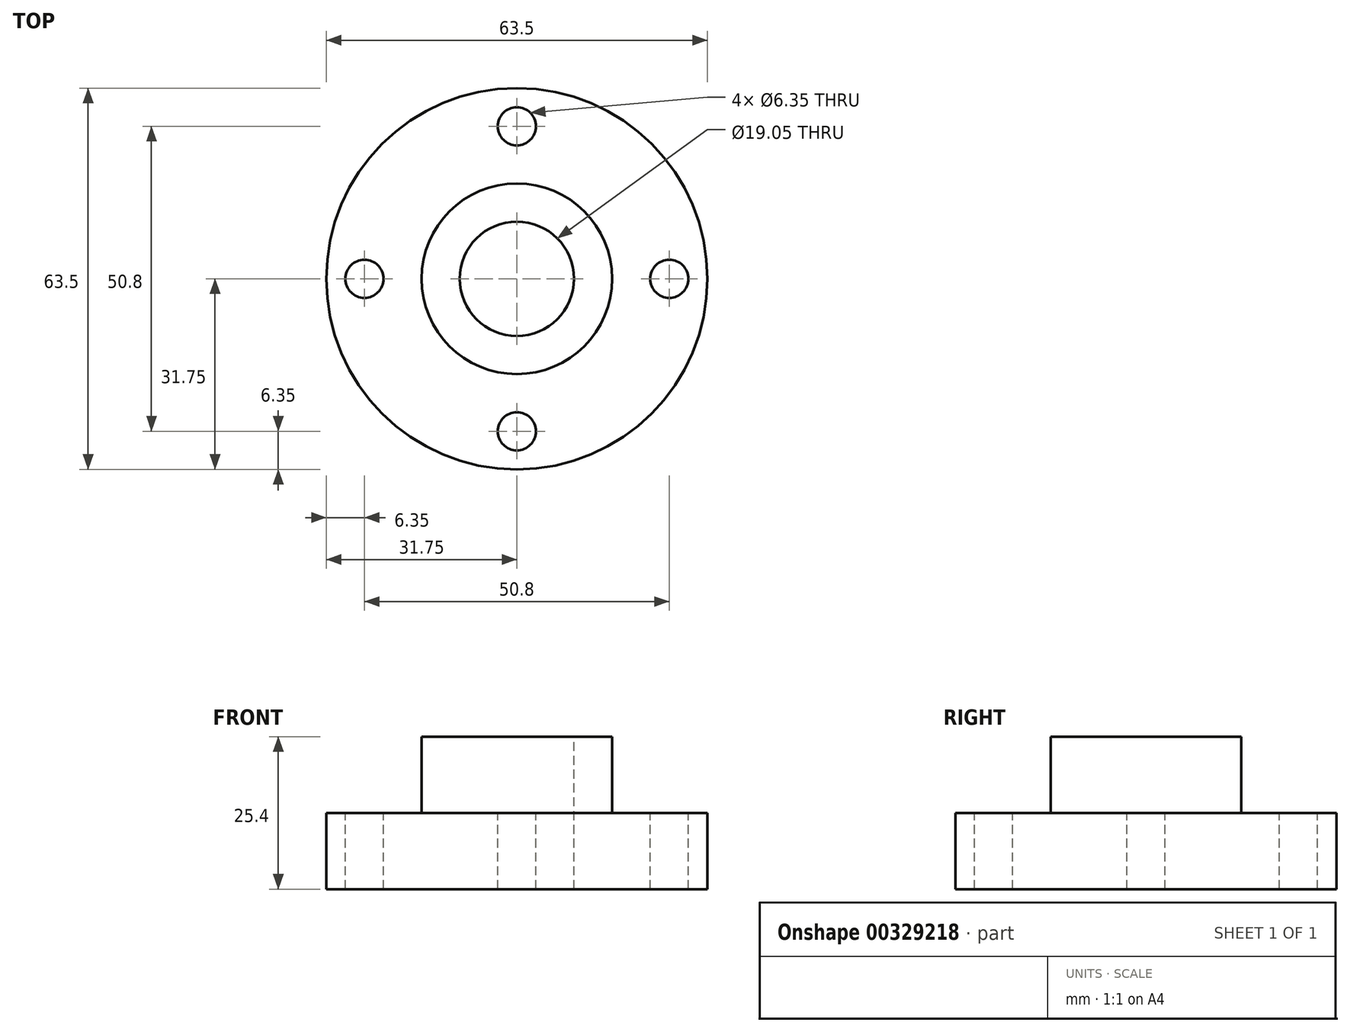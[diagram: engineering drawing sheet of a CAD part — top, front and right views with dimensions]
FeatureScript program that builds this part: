
annotation { "Feature Type Name" : "Feature", "Feature Type Description" : "" }
export const myFeature = defineFeature(function(context is Context, id is Id, definition is map)
    precondition{}
    {
        {
            var Q0;
            Q0=qCreatedBy(makeId("Front.planeOp"),FACE);
            var sketch = newSketch(context, id + "F0", { "sketchPlane" : qUnion([Q0])});
            skLineSegment(sketch, "E0.bottom", {"start": v(0, 0) * mm, "end": v(63.5, 0) * mm});
            skLineSegment(sketch, "E0.top", {"start": v(0, 12.7) * mm, "end": v(63.5, 12.7) * mm});
            skLineSegment(sketch, "E0.left", {"start": v(0, 0) * mm, "end": v(0, 12.7) * mm});
            skLineSegment(sketch, "E0.right", {"start": v(63.5, 0) * mm, "end": v(63.5, 12.7) * mm});
            skLineSegment(sketch, "E1.bottom", {"start": v(15.88, 12.7) * mm, "end": v(47.62, 12.7) * mm});
            skLineSegment(sketch, "E1.top", {"start": v(15.87, 25.4) * mm, "end": v(47.62, 25.4) * mm});
            skLineSegment(sketch, "E1.left", {"start": v(15.88, 12.7) * mm, "end": v(15.87, 25.4) * mm});
            skLineSegment(sketch, "E1.right", {"start": v(47.62, 12.7) * mm, "end": v(47.62, 25.4) * mm});
            skSolve(sketch);
        }
        {
            var Q0;
            Q0=qCreatedBy(makeId("Top.planeOp"),FACE);
            var sketch = newSketch(context, id + "F1", { "sketchPlane" : qUnion([Q0])});
            skCircle(sketch, "E2", {"center": v(0, 0) * mm, "radius": 31.75 * mm});
            skSolve(sketch);
        }
        {
            var Q0;
            Q0 = qSketchRegion(id + "F1", true);
            extrude(context, id + "F2", {"entities" : qUnion([Q0]), "depth" : 12.7 * mm});
        }
        {
            var Q0;
            Q0=makeQuery(id+"F2.opExtrude","CAP_FACE",FACE,{"disambiguationData":[OSD([sQuery(id+"F1.wireOp",EDGE,"E2")])],"isStart":false});
            var sketch = newSketch(context, id + "F3", { "sketchPlane" : qUnion([Q0])});
            skCircle(sketch, "E3", {"center": v(0, 0) * mm, "radius": 15.88 * mm});
            skSolve(sketch);
        }
        {
            var Q0;
            Q0 = qSketchRegion(id + "F3", true);
            extrude(context, id + "F4", {"entities" : qUnion([Q0]), "operationType" : NewBodyOperationType.ADD, "depth" : 12.7 * mm});
        }
        {
            var Q0;
            Q0=makeQuery(id+"F4.opExtrude","CAP_FACE",FACE,{"disambiguationData":[OSD([sQuery(id+"F3.wireOp",EDGE,"E3")])],"isStart":false});
            var sketch = newSketch(context, id + "F5", { "sketchPlane" : qUnion([Q0])});
            skCircle(sketch, "E4", {"center": v(0, 0) * mm, "radius": 9.53 * mm});
            skSolve(sketch);
        }
        {
            var Q0;
            Q0 = qSketchRegion(id + "F5", true);
            extrude(context, id + "F6", {"entities" : qUnion([Q0]), "operationType" : NewBodyOperationType.REMOVE, "endBound" : BoundingType.THROUGH_ALL, "oppositeDirection" : true, "depth" : 25.4 * mm});
        }
        {
            var Q0;
            Q0=makeQuery(id+"F2.opExtrude","CAP_FACE",FACE,{"disambiguationData":[OSD([sQuery(id+"F1.wireOp",EDGE,"E2")])],"isStart":false});
            var sketch = newSketch(context, id + "F7", { "sketchPlane" : qUnion([Q0])});
            skCircle(sketch, "E5", {"center": v(0, 25.4) * mm, "radius": 3.18 * mm});
            skCircle(sketch, "E6", {"center": v(-25.4, 0) * mm, "radius": 3.18 * mm});
            skCircle(sketch, "E7", {"center": v(0, -25.4) * mm, "radius": 3.18 * mm});
            skCircle(sketch, "E8", {"center": v(25.4, 0) * mm, "radius": 3.18 * mm});
            skSolve(sketch);
        }
        {
            var Q0;
            Q0=makeQuery(id+"F7.imprint","IMPRINT",FACE,{"disambiguationData":[TD([[makeQuery(id+"F7.imprint","IMPRINT",EDGE,{"derivedFrom":sQuery(id+"F7.wireOp",EDGE,"E8")}),1.0]])]});
            var Q1;
            Q1=makeQuery(id+"F7.imprint","IMPRINT",FACE,{"disambiguationData":[TD([[makeQuery(id+"F7.imprint","IMPRINT",EDGE,{"derivedFrom":sQuery(id+"F7.wireOp",EDGE,"E7")}),1.0]])]});
            var Q2;
            Q2=makeQuery(id+"F7.imprint","IMPRINT",FACE,{"disambiguationData":[TD([[makeQuery(id+"F7.imprint","IMPRINT",EDGE,{"derivedFrom":sQuery(id+"F7.wireOp",EDGE,"E6")}),1.0]])]});
            var Q3;
            Q3=makeQuery(id+"F7.imprint","IMPRINT",FACE,{"disambiguationData":[TD([[makeQuery(id+"F7.imprint","IMPRINT",EDGE,{"derivedFrom":sQuery(id+"F7.wireOp",EDGE,"E5")}),1.0]])]});
            var Q4;
            Q4=sQuery(id+"F7.wireOp",EDGE,"E7");
            var Q5;
            Q5=sQuery(id+"F7.wireOp",EDGE,"E6");
            var Q6;
            Q6=sQuery(id+"F7.wireOp",EDGE,"E5");
            var Q7;
            Q7=sQuery(id+"F7.wireOp",EDGE,"E8");
            extrude(context, id + "F8", {"entities" : qUnion([Q0, Q1, Q2, Q3]), "operationType" : NewBodyOperationType.REMOVE, "surfaceEntities" : qUnion([Q4, Q5, Q6, Q7]), "endBound" : BoundingType.THROUGH_ALL, "oppositeDirection" : true, "depth" : 25.4 * mm});
        }
    });
